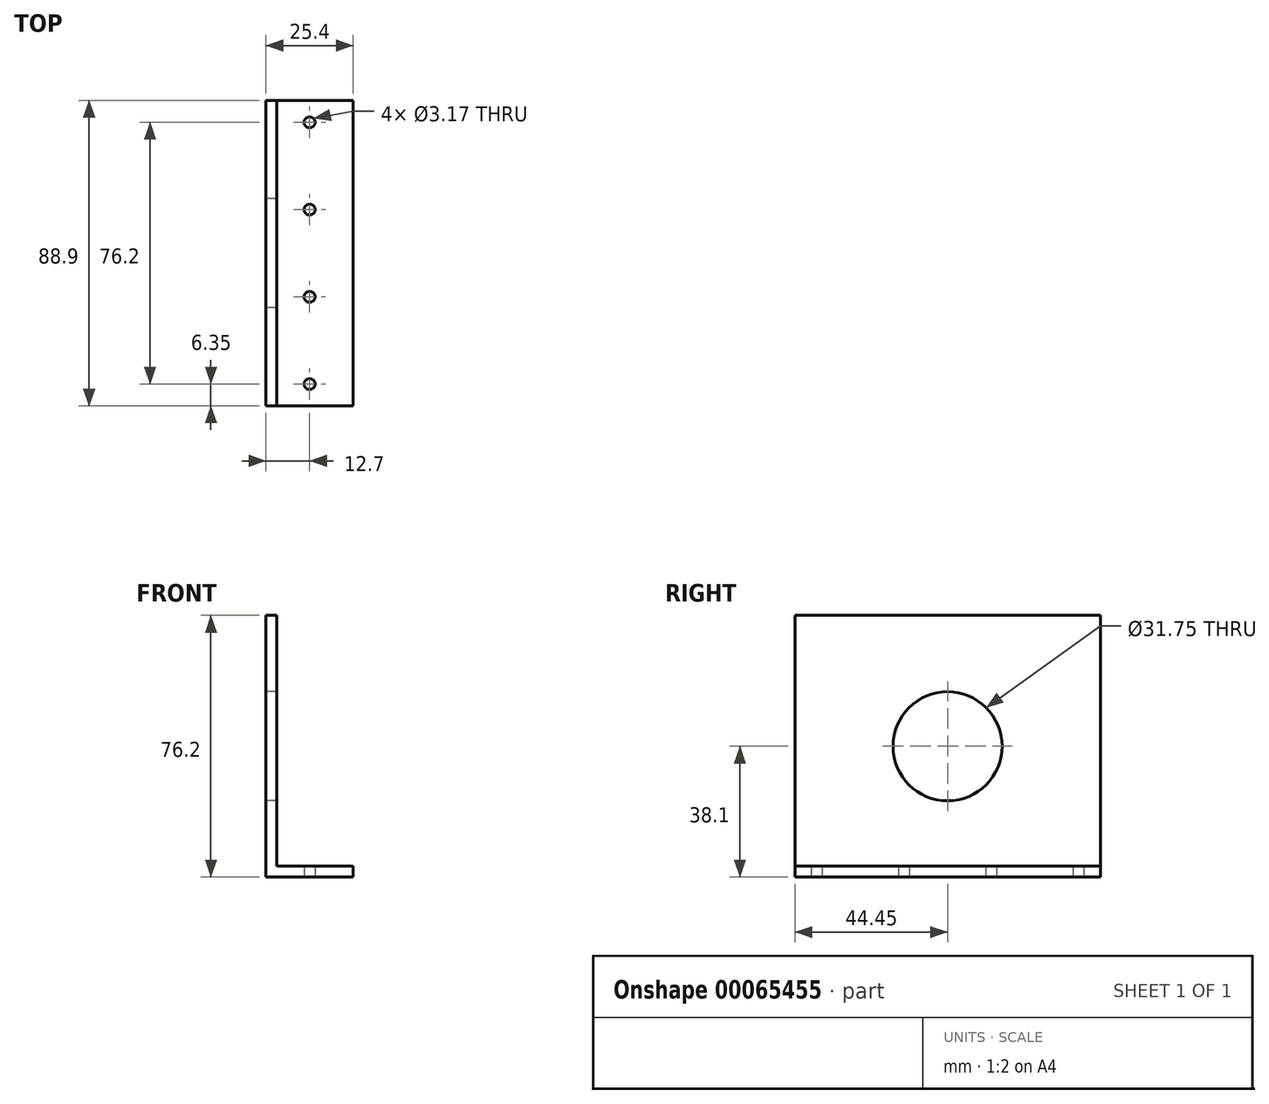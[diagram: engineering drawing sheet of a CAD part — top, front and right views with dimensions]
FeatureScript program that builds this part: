
annotation { "Feature Type Name" : "Feature", "Feature Type Description" : "" }
export const myFeature = defineFeature(function(context is Context, id is Id, definition is map)
    precondition{}
    {
        {
            var Q0;
            Q0=qCreatedBy(makeId("Front.planeOp"),FACE);
            var sketch = newSketch(context, id + "F0", { "sketchPlane" : qUnion([Q0])});
            skLineSegment(sketch, "E0.bottom", {"start": v(0, 0) * mm, "end": v(25.4, 0) * mm});
            skLineSegment(sketch, "E0.top", {"start": v(0, 76.2) * mm, "end": v(3.17, 76.2) * mm});
            skLineSegment(sketch, "E0.left", {"start": v(0, 0) * mm, "end": v(0, 76.2) * mm});
            skLineSegment(sketch, "E0.right", {"start": v(25.4, 0) * mm, "end": v(25.4, 3.17) * mm});
            skLineSegment(sketch, "E1", {"start": v(25.4, 3.17) * mm, "end": v(3.17, 3.17) * mm});
            skLineSegment(sketch, "E2", {"start": v(3.17, 3.17) * mm, "end": v(3.17, 76.2) * mm});
            skLineSegment(sketch, "E3", {"start": v(3.17, 76.2) * mm, "end": v(0, 76.2) * mm});
            skSolve(sketch);
        }
        {
            var Q0;
            Q0=makeQuery(id+"F0.imprint","IMPRINT",FACE,{"disambiguationData":[TD([[makeQuery(id+"F0.imprint","IMPRINT",EDGE,{"derivedFrom":sQuery(id+"F0.wireOp",EDGE,"E0.bottom")}),1.0]])]});
            extrude(context, id + "F1", {"entities" : qUnion([Q0]), "depth" : 88.9 * mm});
        }
        {
            var Q0;
            Q0=makeQuery(id+"F1.opExtrude","SWEPT_FACE",FACE,{"disambiguationData":[OSD([sQuery(id+"F0.wireOp",EDGE,"E0.left")])]});
            var sketch = newSketch(context, id + "F2", { "sketchPlane" : qUnion([Q0])});
            skCircle(sketch, "E4", {"center": v(44.45, 38.1) * mm, "radius": 19.05 * mm});
            skSolve(sketch);
        }
        {
            var Q0;
            Q0=sQuery(id+"F2.wireOp",VERTEX,"E4.center");
            var Q1;
            Q1=makeQuery(id+"F1.opExtrude","SWEPT_BODY",BODY,{"disambiguationData":[OSD([sQuery(id+"F0.wireOp",EDGE,"E0.bottom"),sQuery(id+"F0.wireOp",EDGE,"E0.left"),sQuery(id+"F0.wireOp",EDGE,"E0.right"),sQuery(id+"F0.wireOp",EDGE,"E1"),sQuery(id+"F0.wireOp",EDGE,"E2"),sQuery(id+"F0.wireOp",EDGE,"E3")])]});
            hole(context, id + "F3", {"style" : HoleStyle.SIMPLE, "holeDiameter" : 31.75 * mm, "endStyle" : HoleEndStyle.THROUGH, "locations" : qUnion([Q0]), "scope" : qUnion([Q1])});
        }
        {
            var Q0;
            Q0=makeQuery(id+"F1.opExtrude","SWEPT_FACE",FACE,{"disambiguationData":[OSD([sQuery(id+"F0.wireOp",EDGE,"E0.bottom")])]});
            var sketch = newSketch(context, id + "F4", { "sketchPlane" : qUnion([Q0])});
            skLineSegment(sketch, "E5", {"start": v(12.7, 88.9) * mm, "end": v(12.7, 82.55) * mm});
            skLineSegment(sketch, "E6", {"start": v(12.7, 82.55) * mm, "end": v(12.7, 57.15) * mm});
            skLineSegment(sketch, "E7", {"start": v(12.7, 57.15) * mm, "end": v(12.7, 31.75) * mm});
            skLineSegment(sketch, "E8", {"start": v(12.7, 31.75) * mm, "end": v(12.7, 6.35) * mm});
            skSolve(sketch);
        }
        {
            var Q0;
            Q0=sQuery(id+"F4.wireOp",VERTEX,"E6.start");
            var Q1;
            Q1=sQuery(id+"F4.wireOp",VERTEX,"E6.end");
            var Q2;
            Q2=sQuery(id+"F4.wireOp",VERTEX,"E8.start");
            var Q3;
            Q3=sQuery(id+"F4.wireOp",VERTEX,"E8.end");
            var Q4;
            Q4=makeQuery(id+"F1.opExtrude","SWEPT_BODY",BODY,{"disambiguationData":[OSD([sQuery(id+"F0.wireOp",EDGE,"E0.bottom"),sQuery(id+"F0.wireOp",EDGE,"E0.left"),sQuery(id+"F0.wireOp",EDGE,"E0.right"),sQuery(id+"F0.wireOp",EDGE,"E1"),sQuery(id+"F0.wireOp",EDGE,"E2"),sQuery(id+"F0.wireOp",EDGE,"E3")])]});
            hole(context, id + "F5", {"style" : HoleStyle.SIMPLE, "holeDiameter" : 3.17 * mm, "endStyle" : HoleEndStyle.THROUGH, "locations" : qUnion([Q0, Q1, Q2, Q3]), "scope" : qUnion([Q4])});
        }
    });
